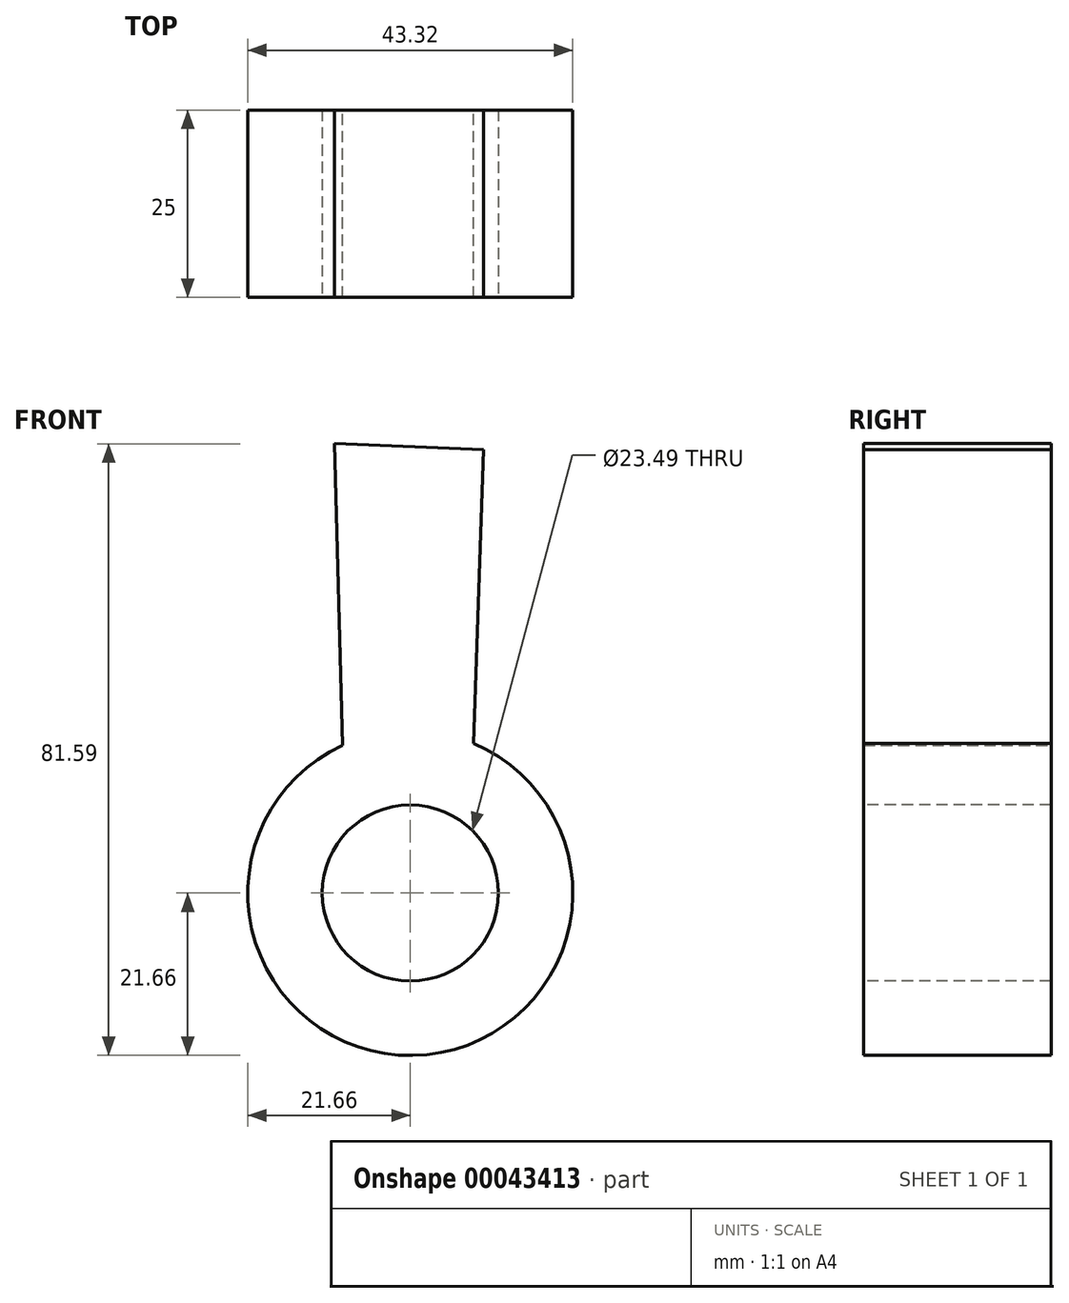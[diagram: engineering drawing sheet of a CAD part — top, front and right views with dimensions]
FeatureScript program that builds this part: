
annotation { "Feature Type Name" : "Feature", "Feature Type Description" : "" }
export const myFeature = defineFeature(function(context is Context, id is Id, definition is map)
    precondition{}
    {
        {
            var Q0;
            Q0=qCreatedBy(makeId("Front.planeOp"),FACE);
            var sketch = newSketch(context, id + "F0", { "sketchPlane" : qUnion([Q0])});
            skArc(sketch, "E0", {"start": v(-9.05, 19.69) * mm, "mid": v(0.33, -21.66) * mm, "end": v(8.44, 19.95) * mm});
            skLineSegment(sketch, "E1", {"start": v(-9.05, 19.69) * mm, "end": v(-10.1, 59.93) * mm});
            skLineSegment(sketch, "E2", {"start": v(-10.1, 59.93) * mm, "end": v(9.74, 59.11) * mm});
            skLineSegment(sketch, "E3", {"start": v(9.74, 59.11) * mm, "end": v(8.44, 19.95) * mm});
            skSolve(sketch);
        }
        {
            var Q0;
            Q0=makeQuery(id+"F0.imprint","IMPRINT",FACE,{"disambiguationData":[TD([[makeQuery(id+"F0.imprint","IMPRINT",EDGE,{"derivedFrom":sQuery(id+"F0.wireOp",EDGE,"E0")}),1.0]])]});
            extrude(context, id + "F1", {"entities" : qUnion([Q0]), "depth" : 25 * mm});
        }
        {
            var Q0;
            Q0=makeQuery(id+"F1.opExtrude","CAP_FACE",FACE,{"disambiguationData":[OSD([sQuery(id+"F0.wireOp",EDGE,"E0"),sQuery(id+"F0.wireOp",EDGE,"E1"),sQuery(id+"F0.wireOp",EDGE,"E2"),sQuery(id+"F0.wireOp",EDGE,"E3")])],"isStart":false});
            var sketch = newSketch(context, id + "F2", { "sketchPlane" : qUnion([Q0])});
            skCircle(sketch, "E4", {"center": v(0, 0) * mm, "radius": 11.74 * mm});
            skSolve(sketch);
        }
        {
            var Q0;
            Q0=makeQuery(id+"F2.imprint","IMPRINT",FACE,{"disambiguationData":[TD([[makeQuery(id+"F2.imprint","IMPRINT",EDGE,{"derivedFrom":sQuery(id+"F2.wireOp",EDGE,"E4")}),1.0]])]});
            extrude(context, id + "F3", {"entities" : qUnion([Q0]), "operationType" : NewBodyOperationType.REMOVE, "endBound" : BoundingType.THROUGH_ALL, "oppositeDirection" : true, "depth" : 25 * mm});
        }
    });
